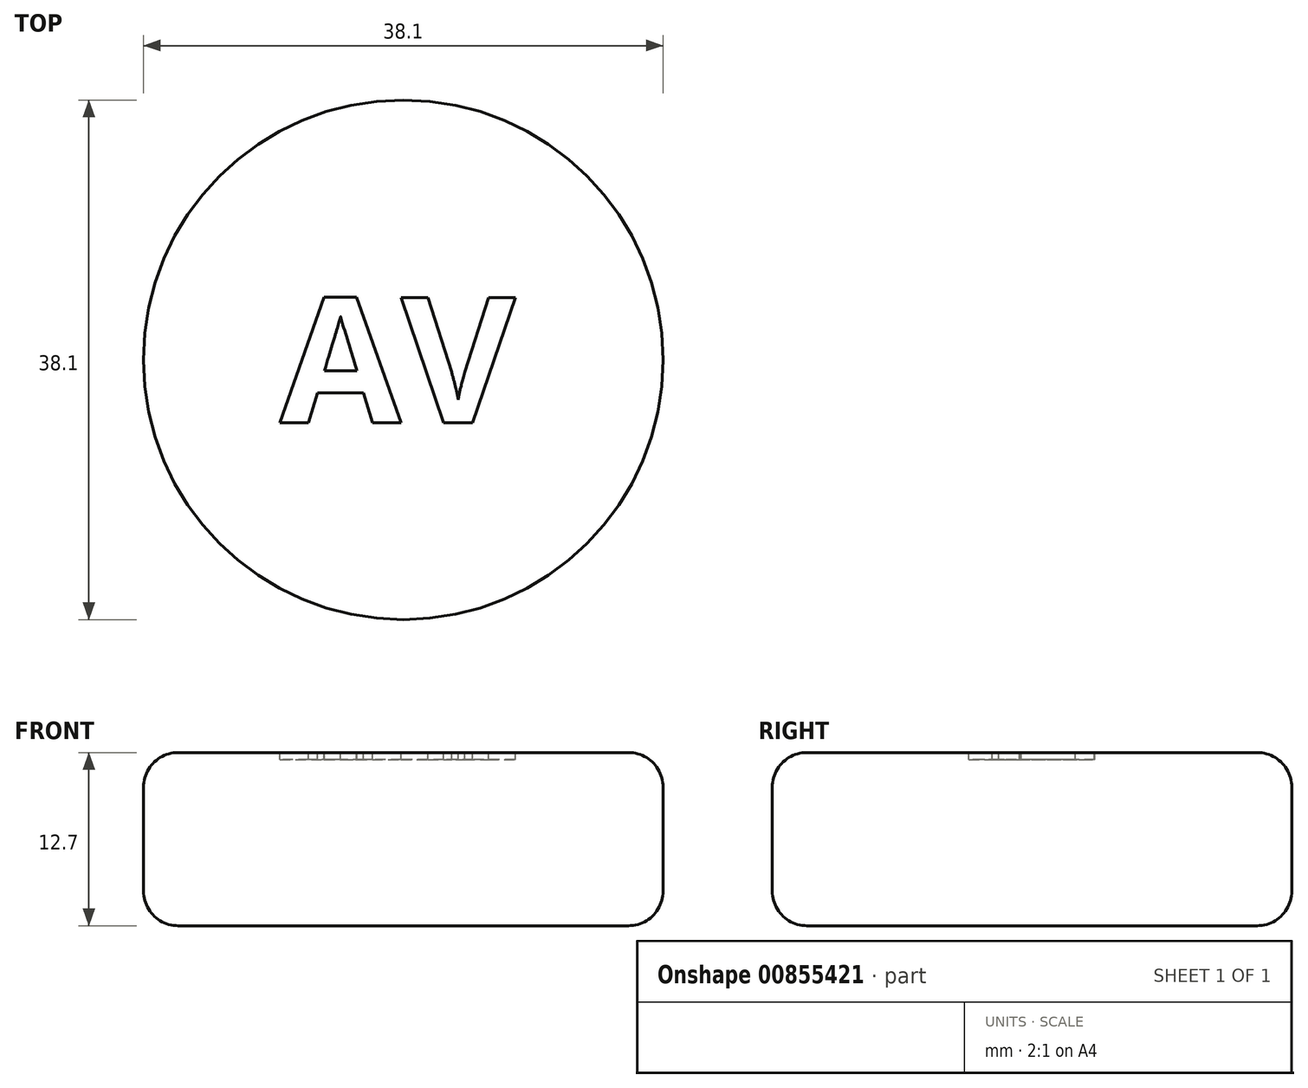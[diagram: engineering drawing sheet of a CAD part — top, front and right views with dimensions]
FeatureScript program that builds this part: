
annotation { "Feature Type Name" : "Feature", "Feature Type Description" : "" }
export const myFeature = defineFeature(function(context is Context, id is Id, definition is map)
    precondition{}
    {
        {
            var Q0;
            Q0=qCreatedBy(makeId("Top.planeOp"),FACE);
            var sketch = newSketch(context, id + "F0", { "sketchPlane" : qUnion([Q0])});
            skCircle(sketch, "E0", {"center": v(0, 0) * mm, "radius": 19.05 * mm});
            skSolve(sketch);
        }
        {
            var Q0;
            Q0=makeQuery(id+"F0.imprint","IMPRINT",FACE,{"disambiguationData":[TD([[makeQuery(id+"F0.imprint","IMPRINT",EDGE,{"derivedFrom":sQuery(id+"F0.wireOp",EDGE,"E0")}),1.0]])]});
            extrude(context, id + "F1", {"entities" : qUnion([Q0]), "depth" : 12.7 * mm, "offsetDistance" : 25.4 * mm});
        }
        {
            var Q0;
            Q0=makeQuery(id+"F1.opExtrude","CAP_EDGE",EDGE,{"disambiguationData":[OSD([sQuery(id+"F0.wireOp",EDGE,"E0")])],"isStart":true});
            var Q1;
            Q1=makeQuery(id+"F1.opExtrude","CAP_EDGE",EDGE,{"disambiguationData":[OSD([sQuery(id+"F0.wireOp",EDGE,"E0")])],"isStart":false});
            fillet(context, id + "F2", {"entities" : qUnion([Q0, Q1]), "radius" : 2.54 * mm, "tangentPropagation" : true, "allowEdgeOverflow" : false});
        }
        {
            var Q0;
            Q0=makeQuery(id+"F1.opExtrude","CAP_FACE",FACE,{"disambiguationData":[OSD([sQuery(id+"F0.wireOp",EDGE,"E0")])],"isStart":false});
            var sketch = newSketch(context, id + "F3", { "sketchPlane" : qUnion([Q0])});
            skText(sketch, "E1", { "text": "AV", "fontName": "OpenSans-Bold.ttf"});
            const initialGuessF3  = {"E1": [-0.00904, -0.00463, 1, 0, 0.00927]};
            skSetInitialGuess(sketch, initialGuessF3);
            skSolve(sketch);
        }
        {
            var Q0;
            Q0 = qSketchRegion(id + "F3", true);
            extrude(context, id + "F4", {"entities" : qUnion([Q0]), "operationType" : NewBodyOperationType.REMOVE, "oppositeDirection" : true, "depth" : 0.5 * mm, "offsetDistance" : 25.4 * mm});
        }
    });
